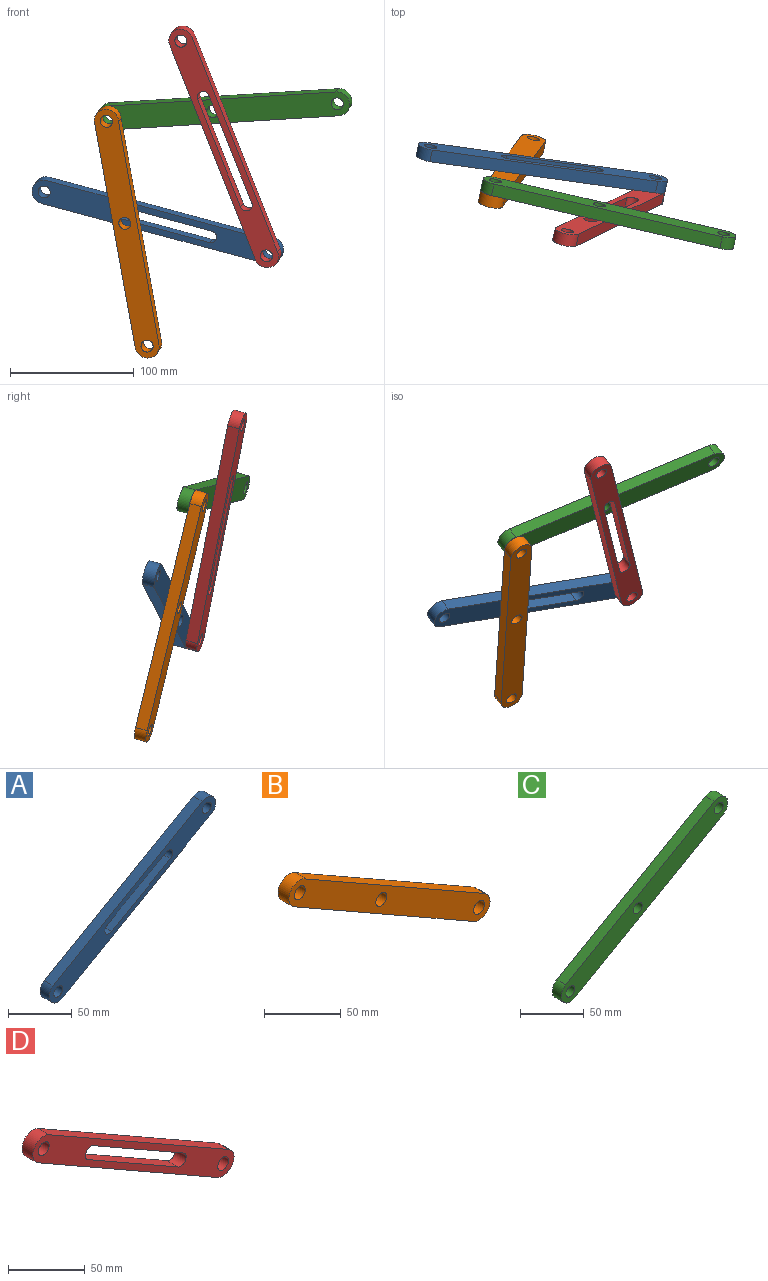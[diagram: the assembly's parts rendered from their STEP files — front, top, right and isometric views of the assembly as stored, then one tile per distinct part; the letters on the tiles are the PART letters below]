
ASSEMBLY  parts=4 mates=4
PART A: 12 faces, bbox 185x10x114.2 mm
  f0: cylinder r=5mm len=10mm, axis (0,-1,0), area 157.1mm2, adj f1,f7,f10,f11
  f1: plane 65.53x37.42mm, normal (0.5,0,-0.87), area 754.6mm2, adj f0,f2,f10,f11
  f2: cylinder r=5mm len=10mm, axis (0,-1,0), area 157.1mm2, adj f1,f7,f10,f11
  f3: plane 166.88x95.6mm, normal (0.5,0,-0.87), area 1923.2mm2, adj f4,f8,f10,f11
  f4: cylinder r=10mm len=17.29mm, axis (0,-1,0), area 290.6mm2, adj f3,f5,f10,f11
  f5: plane 165.65x94.61mm, normal (-0.5,0,0.87), area 1907.7mm2, adj f4,f8,f10,f11
  f6: cylinder r=5mm len=10mm, axis (0,-1,0), area 314.2mm2, adj f10,f11
  f7: plane 65.53x37.42mm, normal (-0.5,0,0.87), area 754.6mm2, adj f0,f2,f10,f11
  f8: cylinder r=10mm len=18.28mm, axis (0,-1,0), area 306.6mm2, adj f3,f5,f10,f11
  f9: cylinder r=5mm len=10mm, axis (0,-1,0), area 314.2mm2, adj f10,f11
  f10: plane 185x114.21mm, normal (0,1,0), area 3094.7mm2, adj f0,f1,f2,f3,f4,f5,f6,f7
  f11: plane 185x114.21mm, normal (0,-1,0), area 3094.7mm2, adj f0,f1,f2,f3,f4,f5,f6,f7
PART B: 9 faces, bbox 185x10x114.2 mm
  f0: plane 163.8x93.4mm, normal (0.5,0,0.87), area 1885.6mm2, adj f1,f5,f7,f8
  f1: cylinder r=10mm len=18.68mm, axis (0,1,0), area 328.5mm2, adj f0,f2,f7,f8
  f2: plane 164.46x93.88mm, normal (-0.5,0,-0.87), area 1893.7mm2, adj f1,f5,f7,f8
  f3: cylinder r=5mm len=10mm, axis (0,1,0), area 314.2mm2, adj f7,f8
  f4: cylinder r=5mm len=10mm, axis (0,1,0), area 314.2mm2, adj f7,f8
  f5: cylinder r=10mm len=18.69mm, axis (0,1,0), area 320.5mm2, adj f0,f2,f7,f8
  f6: cylinder r=5mm len=10mm, axis (0,1,0), area 314.2mm2, adj f7,f8
  f7: plane 185x114.21mm, normal (0,-1,0), area 3866.9mm2, adj f0,f1,f2,f3,f4,f5,f6
  f8: plane 185x114.21mm, normal (0,1,0), area 3866.9mm2, adj f0,f1,f2,f3,f4,f5,f6
PART C: 9 faces, bbox 185x10x114.2 mm
  f0: plane 165x94.21mm, normal (-0.5,0,0.87), area 1900mm2, adj f1,f5,f7,f8
  f1: cylinder r=10mm len=18.68mm, axis (0,-1,0), area 314.2mm2, adj f0,f2,f7,f8
  f2: plane 165x94.21mm, normal (0.5,0,-0.87), area 1900mm2, adj f1,f5,f7,f8
  f3: cylinder r=5mm len=10mm, axis (0,-1,0), area 314.2mm2, adj f7,f8
  f4: cylinder r=4.98mm len=10mm, axis (0,-1,0), area 312.9mm2, adj f7,f8
  f5: cylinder r=10mm len=18.68mm, axis (0,-1,0), area 314.2mm2, adj f0,f2,f7,f8
  f6: cylinder r=5mm len=10mm, axis (0,-1,0), area 314.2mm2, adj f7,f8
  f7: plane 185x114.21mm, normal (0,1,0), area 3879.2mm2, adj f0,f1,f2,f3,f4,f5,f6
  f8: plane 185x114.21mm, normal (0,-1,0), area 3879.2mm2, adj f0,f1,f2,f3,f4,f5,f6
PART D: 14 faces, bbox 185x10x114.2 mm
  f0: cylinder r=5mm len=10mm, axis (0,1,0), area 163mm2, adj f1,f8,f12,f13
  f1: plane 82.18x46.88mm, normal (0.5,0,0.87), area 946.1mm2, adj f0,f2,f12,f13
  f2: cylinder r=5mm len=10mm, axis (0,1,0), area 157.1mm2, adj f1,f8,f12,f13
  f3: plane 165x94.21mm, normal (-0.5,0,-0.87), area 1900mm2, adj f4,f10,f12,f13
  f4: cylinder r=10mm len=10mm, axis (0,1,0), area 80.5mm2, adj f3,f5,f12,f13
  f5: plane 10x4.03mm, normal (0.5,0,-0.87), area 46.4mm2, adj f4,f6,f12,f13
  f6: cylinder r=10mm len=15.97mm, axis (0,1,0), area 186.8mm2, adj f5,f7,f12,f13
  f7: plane 165x94.21mm, normal (0.5,0,0.87), area 1900mm2, adj f6,f10,f12,f13
  f8: plane 82.68x47.21mm, normal (-0.5,0,-0.87), area 952mm2, adj f0,f2,f12,f13
  f9: cylinder r=5mm len=10mm, axis (0,1,0), area 314.2mm2, adj f12,f13
  f10: cylinder r=10mm len=18.68mm, axis (0,1,0), area 314.2mm2, adj f3,f7,f12,f13
  f11: cylinder r=5mm len=10mm, axis (0,1,0), area 314.2mm2, adj f12,f13
  f12: plane 185x114.21mm, normal (0,-1,0), area 2927.3mm2, adj f0,f1,f2,f3,f4,f5,f6,f7
  f13: plane 185x114.21mm, normal (0,1,0), area 2927.3mm2, adj f0,f1,f2,f3,f4,f5,f6,f7
PLACE A rot(axis=(0.4,0.91,-0.11),47.6deg) t=(-117.3,14.97,72.03)mm
PLACE B rot(axis=(0.36,0.93,-0.07),55deg) t=(-158.28,20.29,84.36)mm
PLACE C rot(axis=(0.57,0.78,-0.27),31.2deg) t=(-87.61,7.72,75.17)mm
PLACE D rot(axis=(0.43,0.89,-0.13),44.3deg) t=(-113.92,16.59,63.69)mm
MATE revolute C.f1 <-> B.f1  axis (-0.2,-0.94,-0.26) through (-111.91,-28.48,222.74)mm
MATE pin_slot C.f4 <-> D.f2  axis (-0.2,-0.94,-0.26) through (-27.93,-47.94,227.93)mm
MATE pin_slot A.f0 <-> B.f4  axis (-0.2,-0.94,-0.26) through (-101.84,-9.12,146.06)mm
MATE revolute D.f4 <-> A.f4  axis (0.2,0.94,0.26) through (17.56,-25.68,113.87)mm
